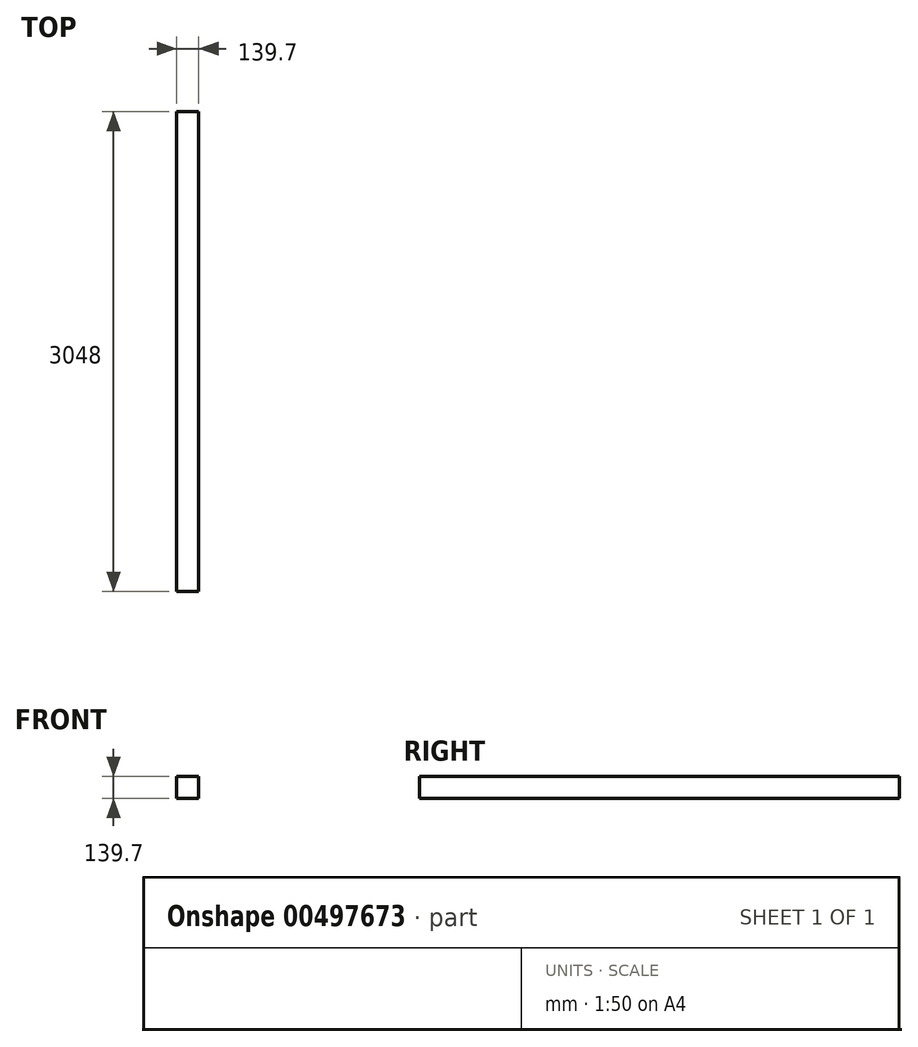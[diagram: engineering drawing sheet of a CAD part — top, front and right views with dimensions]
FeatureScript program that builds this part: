
annotation { "Feature Type Name" : "Feature", "Feature Type Description" : "" }
export const myFeature = defineFeature(function(context is Context, id is Id, definition is map)
    precondition{}
    {
        {
            var Q0;
            Q0=qCreatedBy(makeId("Front.planeOp"),FACE);
            var sketch = newSketch(context, id + "F0", { "sketchPlane" : qUnion([Q0])});
            skLineSegment(sketch, "E0.bottom", {"start": v(0, 0) * mm, "end": v(139.7, 0) * mm});
            skLineSegment(sketch, "E0.top", {"start": v(0, 139.7) * mm, "end": v(139.7, 139.7) * mm});
            skLineSegment(sketch, "E0.left", {"start": v(0, 0) * mm, "end": v(0, 139.7) * mm});
            skLineSegment(sketch, "E0.right", {"start": v(139.7, 0) * mm, "end": v(139.7, 139.7) * mm});
            skSolve(sketch);
        }
        {
            var Q0;
            Q0 = qSketchRegion(id + "F0", true);
            extrude(context, id + "F1", {"entities" : qUnion([Q0]), "depth" : 3048 * mm});
        }
    });
